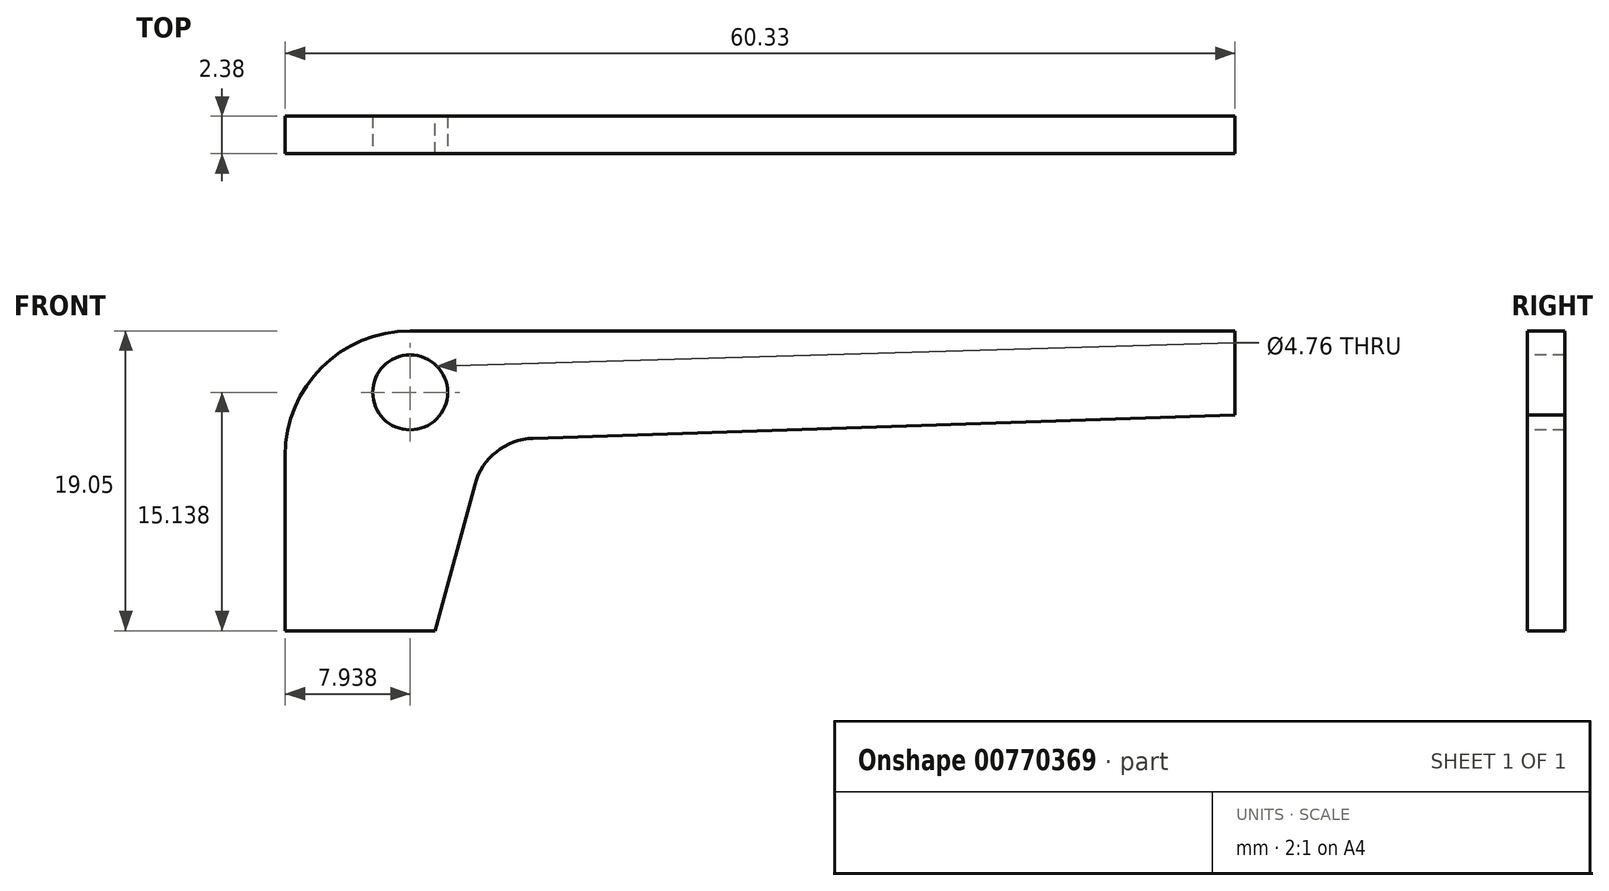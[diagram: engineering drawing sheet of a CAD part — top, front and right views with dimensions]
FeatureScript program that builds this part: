
annotation { "Feature Type Name" : "Feature", "Feature Type Description" : "" }
export const myFeature = defineFeature(function(context is Context, id is Id, definition is map)
    precondition{}
    {
        {
            var Q0;
            Q0=qCreatedBy(makeId("Front.planeOp"),FACE);
            var sketch = newSketch(context, id + "F0", { "sketchPlane" : qUnion([Q0])});
            skLineSegment(sketch, "E0.top", {"start": v(7.94, 19.05) * mm, "end": v(60.33, 19.05) * mm});
            skLineSegment(sketch, "E0.left", {"start": v(0, 0) * mm, "end": v(0, 11.11) * mm});
            skLineSegment(sketch, "E1", {"start": v(9.53, 0) * mm, "end": v(12.04, 9.3) * mm});
            skLineSegment(sketch, "E2", {"start": v(60.33, 13.7) * mm, "end": v(15.74, 12.22) * mm});
            skLineSegment(sketch, "E3", {"start": v(9.53, 0) * mm, "end": v(0, 0) * mm});
            skArc(sketch, "E4", {"start": v(15.74, 12.22) * mm, "mid": v(13.41, 11.36) * mm, "end": v(12.04, 9.3) * mm});
            skPoint(sketch, "E5.visualSharp", {"position": v(0, 19.05) * mm});
            skArc(sketch, "E5.filletArc", {"start": v(7.94, 19.05) * mm, "mid": v(2.32, 16.73) * mm, "end": v(0, 11.11) * mm});
            skLineSegment(sketch, "E6", {"start": v(60.33, 19.05) * mm, "end": v(60.33, 13.7) * mm});
            skSolve(sketch);
        }
        {
            var Q0;
            Q0=makeQuery(id+"F0.imprint","IMPRINT",FACE,{"disambiguationData":[TD([[makeQuery(id+"F0.imprint","IMPRINT",EDGE,{"derivedFrom":sQuery(id+"F0.wireOp",EDGE,"E0.top")}),-1.0]])]});
            extrude(context, id + "F1", {"entities" : qUnion([Q0]), "depth" : 2.38 * mm, "offsetDistance" : 25.4 * mm});
        }
        {
            var Q0;
            Q0=makeQuery(id+"F1.opExtrude","CAP_FACE",FACE,{"disambiguationData":[OSD([sQuery(id+"F0.wireOp",EDGE,"E0.top"),sQuery(id+"F0.wireOp",EDGE,"E0.left"),sQuery(id+"F0.wireOp",EDGE,"E1"),sQuery(id+"F0.wireOp",EDGE,"E2"),sQuery(id+"F0.wireOp",EDGE,"E3"),sQuery(id+"F0.wireOp",EDGE,"E4"),sQuery(id+"F0.wireOp",EDGE,"E5.filletArc"),sQuery(id+"F0.wireOp",EDGE,"E6")])],"isStart":false});
            var sketch = newSketch(context, id + "F2", { "sketchPlane" : qUnion([Q0])});
            skCircle(sketch, "E7", {"center": v(7.94, 15.14) * mm, "radius": 2.38 * mm});
            skSolve(sketch);
        }
        {
            var Q0;
            Q0=makeQuery(id+"F2.imprint","IMPRINT",FACE,{"disambiguationData":[TD([[makeQuery(id+"F2.imprint","IMPRINT",EDGE,{"derivedFrom":sQuery(id+"F2.wireOp",EDGE,"E7")}),1.0]])]});
            extrude(context, id + "F3", {"entities" : qUnion([Q0]), "operationType" : NewBodyOperationType.REMOVE, "endBound" : BoundingType.THROUGH_ALL, "oppositeDirection" : true, "depth" : 25.4 * mm, "offsetDistance" : 25.4 * mm});
        }
    });
